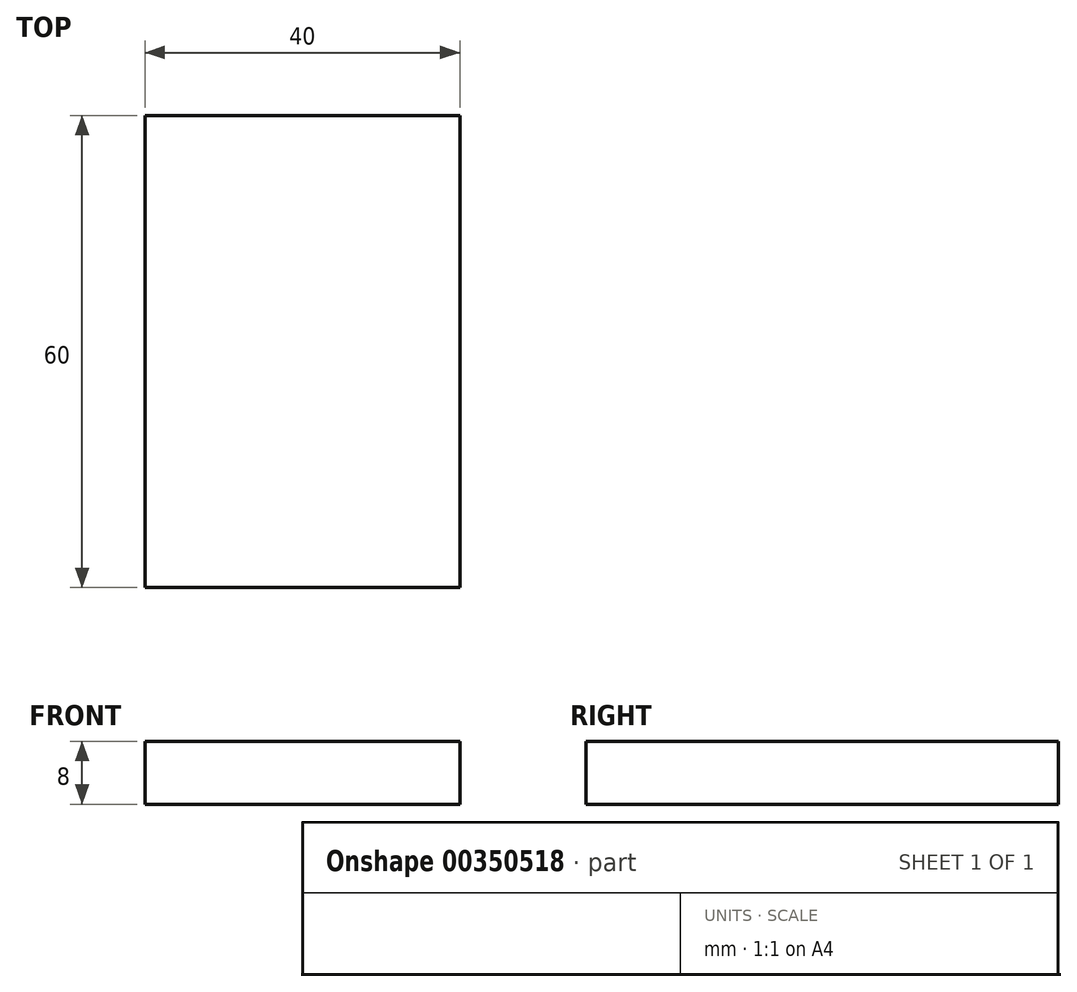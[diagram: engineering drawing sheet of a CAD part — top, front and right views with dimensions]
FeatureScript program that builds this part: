
annotation { "Feature Type Name" : "Feature", "Feature Type Description" : "" }
export const myFeature = defineFeature(function(context is Context, id is Id, definition is map)
    precondition{}
    {
        {
            var Q0;
            Q0=qCreatedBy(makeId("Top.planeOp"),FACE);
            var sketch = newSketch(context, id + "F0", { "sketchPlane" : qUnion([Q0])});
            skLineSegment(sketch, "E0.bottom", {"start": v(-50, 5) * mm, "end": v(50, 5) * mm});
            skLineSegment(sketch, "E0.top", {"start": v(-50, -5) * mm, "end": v(50, -5) * mm});
            skLineSegment(sketch, "E0.left", {"start": v(-50, 5) * mm, "end": v(-50, -5) * mm});
            skLineSegment(sketch, "E0.right", {"start": v(50, 5) * mm, "end": v(50, -5) * mm});
            skPoint(sketch, "E0.middle", {"position": v(0, 0) * mm});
            skSolve(sketch);
        }
        {
            var Q0;
            Q0 = qSketchRegion(id + "F0", true);
            extrude(context, id + "F1", {"entities" : qUnion([Q0]), "depth" : 8 * mm});
        }
        {
            var Q0;
            Q0=makeQuery(id+"F1.opExtrude","SWEPT_FACE",FACE,{"disambiguationData":[OSD([sQuery(id+"F0.wireOp",EDGE,"E0.top")])]});
            extrude(context, id + "F2", {"entities" : qUnion([Q0]), "operationType" : NewBodyOperationType.ADD, "depth" : 50 * mm});
        }
        {
            var Q0;
            {var subQ0=sQuery(id+"F0.wireOp",EDGE,"E0.left");Q0=makeQuery(id+"F2.boolean.opBoolean","MERGE",FACE,{"derivedFrom":[makeQuery(id+"F1.opExtrude","SWEPT_FACE",FACE,{"disambiguationData":[OSD([subQ0])]}),makeQuery(id+"F2.opExtrude","SWEPT_FACE",FACE,{"disambiguationData":[OSD([sQuery(id+"F0.wireOp",EDGE,"E0.top"),subQ0])]})]});}
            extrude(context, id + "F3", {"entities" : qUnion([Q0]), "operationType" : NewBodyOperationType.REMOVE, "oppositeDirection" : true, "depth" : 60 * mm});
        }
    });
